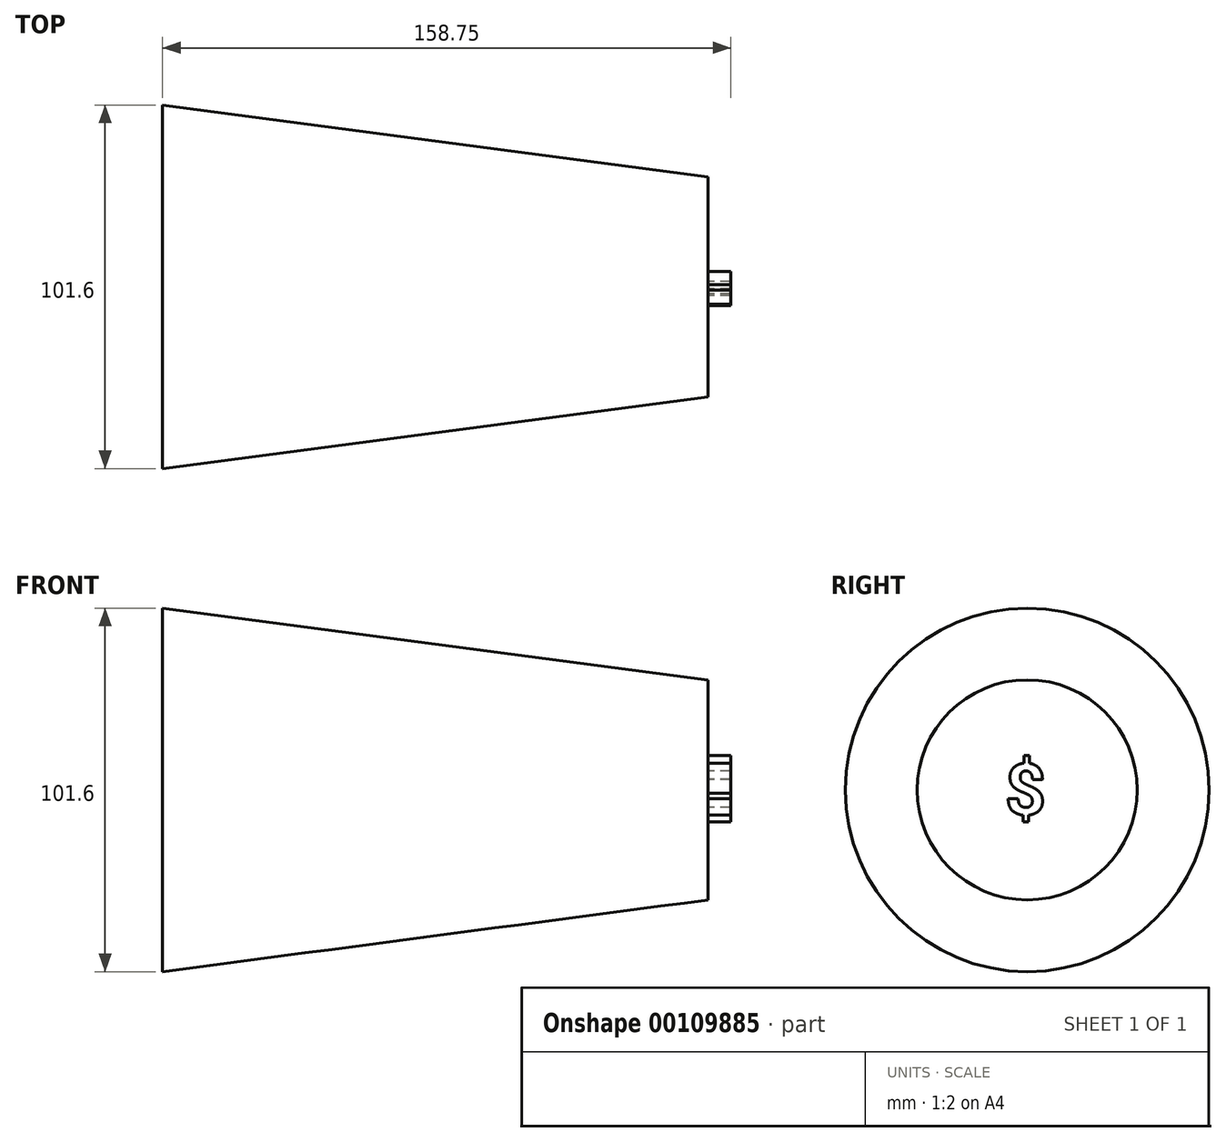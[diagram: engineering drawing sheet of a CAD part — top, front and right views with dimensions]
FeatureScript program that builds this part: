
annotation { "Feature Type Name" : "Feature", "Feature Type Description" : "" }
export const myFeature = defineFeature(function(context is Context, id is Id, definition is map)
    precondition{}
    {
        {
            var Q0;
            Q0=qCreatedBy(makeId("Right.planeOp"),FACE);
            var sketch = newSketch(context, id + "F0", { "sketchPlane" : qUnion([Q0])});
            skCircle(sketch, "E0", {"center": v(0, 0) * mm, "radius": 50.8 * mm});
            skSolve(sketch);
        }
        {
            var Q0;
            Q0=makeQuery(id+"F0.imprint","IMPRINT",FACE,{"disambiguationData":[TD([[makeQuery(id+"F0.imprint","IMPRINT",EDGE,{"derivedFrom":sQuery(id+"F0.wireOp",EDGE,"E0")}),1.0]])]});
            extrude(context, id + "F1", {"entities" : qUnion([Q0]), "depth" : 152.4 * mm, "hasDraft" : true, "draftAngle" : 7.5 * degree, "draftPullDirection" : true});
        }
        {
            var Q0;
            Q0=makeQuery(id+"F1.opExtrude","CAP_FACE",FACE,{"disambiguationData":[OSD([sQuery(id+"F0.wireOp",EDGE,"E0")])],"isStart":false});
            var sketch = newSketch(context, id + "F2", { "sketchPlane" : qUnion([Q0])});
            skText(sketch, "E1", { "text": "$", "fontName": "RobotoSlab-Bold.ttf"});
            const initialGuessF2  = {"E1": [-0.00587, -0.0069, 1, 0, 0.01437]};
            skSetInitialGuess(sketch, initialGuessF2);
            skSolve(sketch);
        }
        {
            var Q0;
            Q0 = qSketchRegion(id + "F2", true);
            extrude(context, id + "F3", {"entities" : qUnion([Q0]), "operationType" : NewBodyOperationType.ADD, "depth" : 6.35 * mm});
        }
    });
